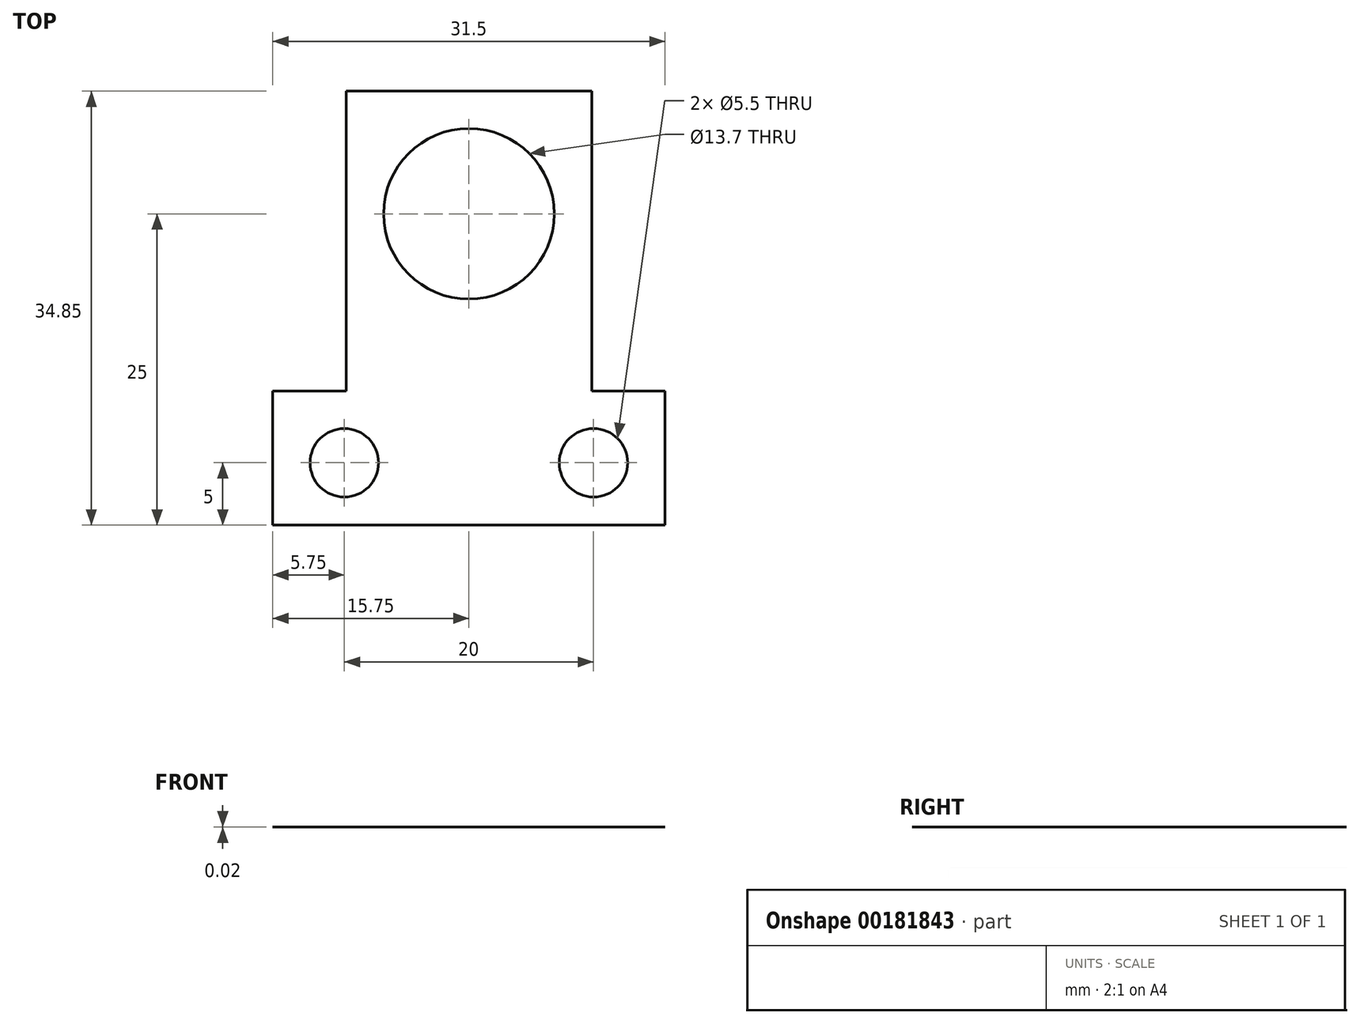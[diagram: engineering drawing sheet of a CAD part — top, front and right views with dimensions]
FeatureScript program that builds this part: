
annotation { "Feature Type Name" : "Feature", "Feature Type Description" : "" }
export const myFeature = defineFeature(function(context is Context, id is Id, definition is map)
    precondition{}
    {
        {
            var Q0;
            Q0=qCreatedBy(makeId("Top.planeOp"),FACE);
            var sketch = newSketch(context, id + "F0", { "sketchPlane" : qUnion([Q0])});
            skLineSegment(sketch, "E0.bottom", {"start": v(-15.75, -25) * mm, "end": v(15.75, -25) * mm});
            skLineSegment(sketch, "E0.top", {"start": v(-9.85, 9.85) * mm, "end": v(9.85, 9.85) * mm});
            skLineSegment(sketch, "E0.left", {"start": v(-15.75, -25) * mm, "end": v(-15.75, -14.25) * mm});
            skLineSegment(sketch, "E0.right", {"start": v(15.75, -25) * mm, "end": v(15.75, -14.25) * mm});
            skLineSegment(sketch, "E1", {"start": v(-15.75, -20) * mm, "end": v(15.75, -20) * mm, "construction": true});
            skCircle(sketch, "E2", {"center": v(-10, -20) * mm, "radius": 2.75 * mm});
            skCircle(sketch, "E3", {"center": v(10, -20) * mm, "radius": 2.75 * mm});
            skLineSegment(sketch, "E4", {"start": v(0, 9.85) * mm, "end": v(0, -25) * mm, "construction": true});
            skLineSegment(sketch, "E5", {"start": v(9.85, 0) * mm, "end": v(-9.85, 0) * mm, "construction": true});
            skCircle(sketch, "E6", {"center": v(0, 0) * mm, "radius": 6.85 * mm});
            skLineSegment(sketch, "E7", {"start": v(-5, -4.68) * mm, "end": v(-5, -25) * mm});
            skLineSegment(sketch, "E8", {"start": v(5, -4.68) * mm, "end": v(5, -25) * mm});
            skLineSegment(sketch, "E9", {"start": v(-6.85, 0) * mm, "end": v(-6.85, -25) * mm});
            skLineSegment(sketch, "E10", {"start": v(6.85, 0) * mm, "end": v(6.85, -25) * mm});
            skLineSegment(sketch, "E11", {"start": v(-15.75, -14.25) * mm, "end": v(15.75, -14.25) * mm});
            skLineSegment(sketch, "E12", {"start": v(-9.85, 9.85) * mm, "end": v(-9.85, -14.25) * mm});
            skLineSegment(sketch, "E13", {"start": v(9.85, 9.85) * mm, "end": v(9.85, -14.25) * mm});
            skSolve(sketch);
        }
        {
            var Q0;
            Q0 = qSketchRegion(id + "F0", true);
            var Q1;
            {var subQ0=sQuery(id+"F0.wireOp",EDGE,"E7");var subQ1=sQuery(id+"F0.wireOp",EDGE,"E6");var subQ2=makeQuery(id+"F0.imprint","INTERSECT",VERTEX,{"derivedFrom":[subQ1,subQ0]});Q1=makeQuery(id+"F0.imprint","IMPRINT",FACE,{"disambiguationData":[TD([[makeQuery(id+"F0.imprint","IMPRINT",EDGE,{"disambiguationData":[TD([[subQ2,1.0]])],"derivedFrom":subQ1}),-1.0]])]});}
            var Q2;
            {var subQ0=sQuery(id+"F0.wireOp",EDGE,"E8");var subQ1=sQuery(id+"F0.wireOp",EDGE,"E6");var subQ2=makeQuery(id+"F0.imprint","INTERSECT",VERTEX,{"derivedFrom":[subQ1,subQ0]});Q2=makeQuery(id+"F0.imprint","IMPRINT",FACE,{"disambiguationData":[TD([[makeQuery(id+"F0.imprint","IMPRINT",EDGE,{"disambiguationData":[TD([[subQ2,-1.0]])],"derivedFrom":subQ1}),-1.0]])]});}
            var Q3;
            {var subQ0=sQuery(id+"F0.wireOp",EDGE,"E7");var subQ1=sQuery(id+"F0.wireOp",EDGE,"E6");var subQ2=makeQuery(id+"F0.imprint","INTERSECT",VERTEX,{"derivedFrom":[subQ1,subQ0]});Q3=makeQuery(id+"F0.imprint","IMPRINT",FACE,{"disambiguationData":[TD([[makeQuery(id+"F0.imprint","IMPRINT",EDGE,{"disambiguationData":[TD([[subQ2,-1.0]])],"derivedFrom":subQ1}),-1.0]])]});}
            extrude(context, id + "F1", {"entities" : qUnion([Q0, Q1, Q2, Q3]), "oppositeDirection" : true, "depth" : 1 / 50.8 * mm});
        }
    });
